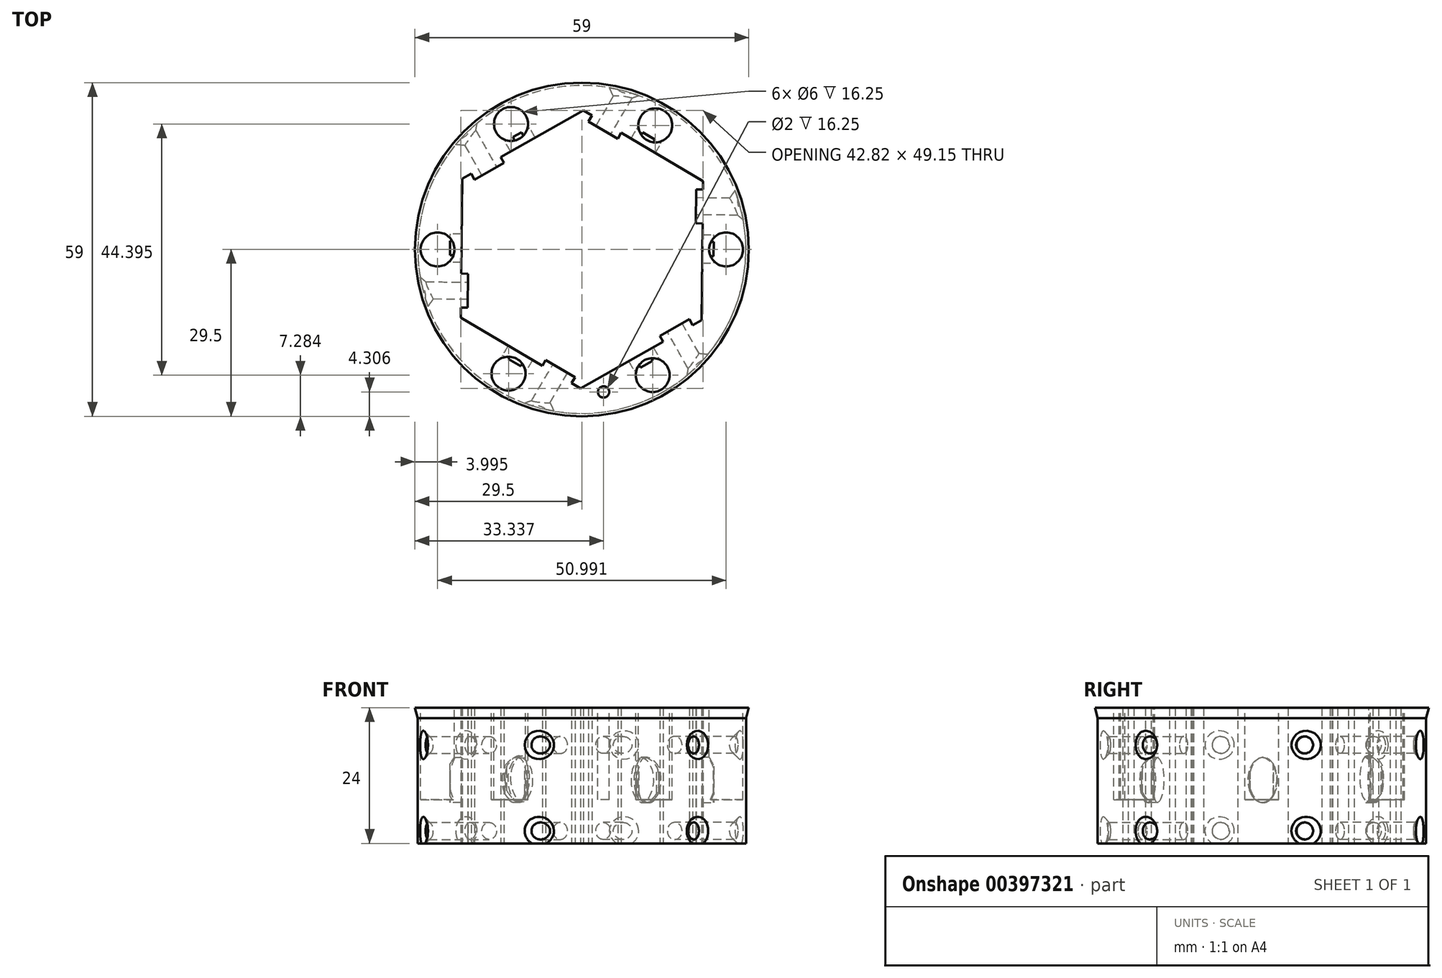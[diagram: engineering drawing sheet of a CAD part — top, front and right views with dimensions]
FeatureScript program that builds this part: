
annotation { "Feature Type Name" : "Feature", "Feature Type Description" : "" }
export const myFeature = defineFeature(function(context is Context, id is Id, definition is map)
    precondition{}
    {
        {
            var Q0;
            Q0=qCreatedBy(makeId("Top.planeOp"),FACE);
            var sketch = newSketch(context, id + "F0", { "sketchPlane" : qUnion([Q0])});
            skCircle(sketch, "E0", {"center": v(0, 0) * mm, "radius": 29 * mm});
            skCircle(sketch, "E1.cCircle", {"center": v(0, 0) * mm, "radius": 24.58 * mm, "construction": true});
            skLineSegment(sketch, "E1.0", {"start": v(-21.4, -12.07) * mm, "end": v(-21.16, 12.5) * mm});
            skLineSegment(sketch, "E1.1", {"start": v(-21.16, 12.5) * mm, "end": v(0.25, 24.58) * mm});
            skLineSegment(sketch, "E1.2", {"start": v(0.25, 24.58) * mm, "end": v(21.4, 12.07) * mm});
            skLineSegment(sketch, "E1.3", {"start": v(21.4, 12.07) * mm, "end": v(21.16, -12.5) * mm});
            skLineSegment(sketch, "E1.4", {"start": v(21.16, -12.5) * mm, "end": v(-0.25, -24.58) * mm});
            skLineSegment(sketch, "E1.5", {"start": v(-0.25, -24.58) * mm, "end": v(-21.4, -12.07) * mm});
            skSolve(sketch);
        }
        {
            var Q0;
            Q0=makeQuery(id+"F0.imprint","IMPRINT",FACE,{"disambiguationData":[TD([[makeQuery(id+"F0.imprint","IMPRINT",EDGE,{"derivedFrom":sQuery(id+"F0.wireOp",EDGE,"E0")}),1.0]])]});
            extrude(context, id + "F1", {"entities" : qUnion([Q0]), "depth" : 22 * mm});
        }
        {
            var Q0;
            Q0=makeQuery(id+"F1.opExtrude","CAP_FACE",FACE,{"disambiguationData":[OSD([sQuery(id+"F0.wireOp",EDGE,"E0"),sQuery(id+"F0.wireOp",EDGE,"E1.0"),sQuery(id+"F0.wireOp",EDGE,"E1.1"),sQuery(id+"F0.wireOp",EDGE,"E1.2"),sQuery(id+"F0.wireOp",EDGE,"E1.3"),sQuery(id+"F0.wireOp",EDGE,"E1.4"),sQuery(id+"F0.wireOp",EDGE,"E1.5")])],"isStart":false});
            var sketch = newSketch(context, id + "F2", { "sketchPlane" : qUnion([Q0])});
            skCircle(sketch, "E2.0", {"center": v(0, 0) * mm, "radius": 29.5 * mm});
            skSolve(sketch);
        }
        {
            var Q0;
            Q0=makeQuery(id+"F2.imprint","IMPRINT",FACE,{"disambiguationData":[TD([[makeQuery(id+"F2.imprint","IMPRINT",EDGE,{"derivedFrom":makeQuery(id+"F1.opExtrude","CAP_EDGE",EDGE,{"disambiguationData":[OSD([sQuery(id+"F0.wireOp",EDGE,"E0")])],"isStart":false})}),1.0]])]});
            var Q1;
            Q1=makeQuery(id+"F2.imprint","IMPRINT",FACE,{"disambiguationData":[TD([[makeQuery(id+"F2.imprint","IMPRINT",EDGE,{"derivedFrom":sQuery(id+"F2.wireOp",EDGE,"E2.0")}),1.0]])]});
            extrude(context, id + "F3", {"entities" : qUnion([Q0, Q1]), "operationType" : NewBodyOperationType.ADD, "depth" : 2 * mm});
        }
        {
            var Q0;
            Q0=makeQuery(id+"F3.opExtrude","CAP_FACE",FACE,{"disambiguationData":[OSD([sQuery(id+"F0.wireOp",EDGE,"E1.0"),sQuery(id+"F0.wireOp",EDGE,"E1.1"),sQuery(id+"F0.wireOp",EDGE,"E1.2"),sQuery(id+"F0.wireOp",EDGE,"E1.3"),sQuery(id+"F0.wireOp",EDGE,"E1.4"),sQuery(id+"F0.wireOp",EDGE,"E1.5"),sQuery(id+"F2.wireOp",EDGE,"E2.0")])],"isStart":false});
            var sketch = newSketch(context, id + "F4", { "sketchPlane" : qUnion([Q0])});
            skCircle(sketch, "E3", {"center": v(-12.53, 22.18) * mm, "radius": 3 * mm});
            skCircle(sketch, "E4", {"center": v(-25.5, 0) * mm, "radius": 3 * mm});
            skCircle(sketch, "E5", {"center": v(-12.97, -21.96) * mm, "radius": 3 * mm});
            skCircle(sketch, "E6", {"center": v(12.52, -22.22) * mm, "radius": 3 * mm});
            skCircle(sketch, "E7", {"center": v(25.49, 0) * mm, "radius": 3 * mm});
            skCircle(sketch, "E8", {"center": v(12.97, 21.94) * mm, "radius": 3 * mm});
            skCircle(sketch, "E9", {"center": v(3.84, -25.2) * mm, "radius": 1 * mm});
            skSolve(sketch);
        }
        {
            var Q0;
            Q0=makeQuery(id+"F4.imprint","IMPRINT",FACE,{"disambiguationData":[TD([[makeQuery(id+"F4.imprint","IMPRINT",EDGE,{"derivedFrom":sQuery(id+"F4.wireOp",EDGE,"E6")}),1.0]])]});
            var Q1;
            Q1=makeQuery(id+"F4.imprint","IMPRINT",FACE,{"disambiguationData":[TD([[makeQuery(id+"F4.imprint","IMPRINT",EDGE,{"derivedFrom":sQuery(id+"F4.wireOp",EDGE,"E5")}),1.0]])]});
            var Q2;
            Q2=makeQuery(id+"F4.imprint","IMPRINT",FACE,{"disambiguationData":[TD([[makeQuery(id+"F4.imprint","IMPRINT",EDGE,{"derivedFrom":sQuery(id+"F4.wireOp",EDGE,"E4")}),1.0]])]});
            var Q3;
            Q3=makeQuery(id+"F4.imprint","IMPRINT",FACE,{"disambiguationData":[TD([[makeQuery(id+"F4.imprint","IMPRINT",EDGE,{"derivedFrom":sQuery(id+"F4.wireOp",EDGE,"E3")}),1.0]])]});
            var Q4;
            Q4=makeQuery(id+"F4.imprint","IMPRINT",FACE,{"disambiguationData":[TD([[makeQuery(id+"F4.imprint","IMPRINT",EDGE,{"derivedFrom":sQuery(id+"F4.wireOp",EDGE,"E8")}),1.0]])]});
            var Q5;
            Q5=makeQuery(id+"F4.imprint","IMPRINT",FACE,{"disambiguationData":[TD([[makeQuery(id+"F4.imprint","IMPRINT",EDGE,{"derivedFrom":sQuery(id+"F4.wireOp",EDGE,"E7")}),1.0]])]});
            var Q6;
            Q6=makeQuery(id+"F4.imprint","IMPRINT",FACE,{"disambiguationData":[TD([[makeQuery(id+"F4.imprint","IMPRINT",EDGE,{"derivedFrom":sQuery(id+"F4.wireOp",EDGE,"E9")}),1.0]])]});
            var Q7;
            Q7=sQuery(id+"F4.wireOp",EDGE,"E3");
            var Q8;
            Q8=sQuery(id+"F4.wireOp",EDGE,"E5");
            var Q9;
            Q9=sQuery(id+"F4.wireOp",EDGE,"E9");
            var Q10;
            Q10=sQuery(id+"F4.wireOp",EDGE,"E6");
            var Q11;
            Q11=sQuery(id+"F4.wireOp",EDGE,"E7");
            var Q12;
            Q12=sQuery(id+"F4.wireOp",EDGE,"E8");
            var Q13;
            Q13=sQuery(id+"F4.wireOp",EDGE,"E4");
            extrude(context, id + "F5", {"entities" : qUnion([Q0, Q1, Q2, Q3, Q4, Q5, Q6]), "operationType" : NewBodyOperationType.REMOVE, "surfaceEntities" : qUnion([Q7, Q8, Q9, Q10, Q11, Q12, Q13]), "oppositeDirection" : true, "depth" : 16.25 * mm});
        }
        {
            var Q0;
            {var subQ0=sQuery(id+"F0.wireOp",EDGE,"E1.4");Q0=makeQuery(id+"F3.boolean.opBoolean","MERGE",FACE,{"derivedFrom":[makeQuery(id+"F1.opExtrude","SWEPT_FACE",FACE,{"disambiguationData":[OSD([subQ0])]}),makeQuery(id+"F3.opExtrude","SWEPT_FACE",FACE,{"disambiguationData":[OSD([subQ0])]})]});}
            var sketch = newSketch(context, id + "F6", { "sketchPlane" : qUnion([Q0])});
            skLineSegment(sketch, "E10", {"start": v(0, 24) * mm, "end": v(0, -1.6) * mm, "construction": true});
            skPoint(sketch, "E10.endSnap0", {"position": v(0, 24) * mm});
            skEllipse(sketch, "E11", {"center": v(0, 11.2) * mm, "majorRadius": 4 * mm, "minorRadius": 2.5 * mm, "majorAxis": v(0, 1)});
            skLineSegment(sketch, "E12", {"start": v(-7.5, 24) * mm, "end": v(-7.5, 0) * mm, "construction": true});
            skCircle(sketch, "E13", {"center": v(-7.5, 17.4) * mm, "radius": 1.5 * mm});
            skCircle(sketch, "E14", {"center": v(-7.5, 2.2) * mm, "radius": 1.5 * mm});
            skSolve(sketch);
        }
        {
            var Q0;
            Q0=makeQuery(id+"F6.imprint","IMPRINT",FACE,{"disambiguationData":[TD([[makeQuery(id+"F6.imprint","IMPRINT",EDGE,{"derivedFrom":sQuery(id+"F6.wireOp",EDGE,"E11")}),1.0]])]});
            var Q1;
            Q1=sQuery(id+"F6.wireOp",EDGE,"E13");
            extrude(context, id + "F7", {"entities" : qUnion([Q0]), "operationType" : NewBodyOperationType.REMOVE, "surfaceEntities" : qUnion([Q1]), "oppositeDirection" : true, "depth" : 2 * mm});
        }
        {
            var Q0;
            {var subQ0=sQuery(id+"F0.wireOp",EDGE,"E1.4");Q0=makeQuery(id+"F3.boolean.opBoolean","MERGE",FACE,{"derivedFrom":[makeQuery(id+"F1.opExtrude","SWEPT_FACE",FACE,{"disambiguationData":[OSD([subQ0])]}),makeQuery(id+"F3.opExtrude","SWEPT_FACE",FACE,{"disambiguationData":[OSD([subQ0])]})]});}
            var sketch = newSketch(context, id + "F8", { "sketchPlane" : qUnion([Q0])});
            skPoint(sketch, "E15.1", {"position": v(0, 24) * mm});
            skCircle(sketch, "E15.4", {"center": v(-7.5, 17.4) * mm, "radius": 1.5 * mm});
            skCircle(sketch, "E15.5", {"center": v(-7.5, 2.2) * mm, "radius": 1.5 * mm});
            skSolve(sketch);
        }
        {
            var Q0;
            Q0=makeQuery(id+"F8.imprint","IMPRINT",FACE,{"disambiguationData":[TD([[makeQuery(id+"F8.imprint","IMPRINT",EDGE,{"derivedFrom":sQuery(id+"F8.wireOp",EDGE,"E15.5")}),1.0]])]});
            var Q1;
            Q1=makeQuery(id+"F8.imprint","IMPRINT",FACE,{"disambiguationData":[TD([[makeQuery(id+"F8.imprint","IMPRINT",EDGE,{"derivedFrom":sQuery(id+"F8.wireOp",EDGE,"E15.4")}),1.0]])]});
            extrude(context, id + "F9", {"entities" : qUnion([Q0, Q1]), "operationType" : NewBodyOperationType.REMOVE, "oppositeDirection" : true, "depth" : 10 * mm, "hasSecondDirection" : true, "secondDirectionOppositeDirection" : false, "secondDirectionDepth" : 5 * mm});
        }
        {
            var Q0;
            {var subQ0=sQuery(id+"F0.wireOp",EDGE,"E1.4");Q0=makeQuery(id+"F3.boolean.opBoolean","MERGE",FACE,{"derivedFrom":[makeQuery(id+"F1.opExtrude","SWEPT_FACE",FACE,{"disambiguationData":[OSD([subQ0])]}),makeQuery(id+"F3.opExtrude","SWEPT_FACE",FACE,{"disambiguationData":[OSD([subQ0])]})]});}
            var sketch = newSketch(context, id + "F10", { "sketchPlane" : qUnion([Q0])});
            skLineSegment(sketch, "E16.bottom", {"start": v(-4.5, 24) * mm, "end": v(-10.5, 24) * mm});
            skLineSegment(sketch, "E16.top", {"start": v(-4.5, 0) * mm, "end": v(-10.5, 0) * mm});
            skLineSegment(sketch, "E16.left", {"start": v(-4.5, 24) * mm, "end": v(-4.5, 0) * mm});
            skLineSegment(sketch, "E16.right", {"start": v(-10.5, 24) * mm, "end": v(-10.5, 0) * mm});
            skSolve(sketch);
        }
        {
            var Q0;
            Q0=makeQuery(id+"F10.imprint","IMPRINT",FACE,{"disambiguationData":[TD([[makeQuery(id+"F10.imprint","IMPRINT",EDGE,{"derivedFrom":sQuery(id+"F10.wireOp",EDGE,"E16.bottom")}),-1.0]])]});
            extrude(context, id + "F11", {"entities" : qUnion([Q0]), "operationType" : NewBodyOperationType.ADD, "depth" : 1.2 * mm});
        }
        {
            var Q0;
            {var subQ0=sQuery(id+"F0.wireOp",EDGE,"E1.5");Q0=makeQuery(id+"F3.boolean.opBoolean","MERGE",FACE,{"derivedFrom":[makeQuery(id+"F1.opExtrude","SWEPT_FACE",FACE,{"disambiguationData":[OSD([subQ0])]}),makeQuery(id+"F3.opExtrude","SWEPT_FACE",FACE,{"disambiguationData":[OSD([subQ0])]})]});}
            var sketch = newSketch(context, id + "F12", { "sketchPlane" : qUnion([Q0])});
            skLineSegment(sketch, "E17", {"start": v(0, 24) * mm, "end": v(0, 0) * mm, "construction": true});
            skLineSegment(sketch, "E18", {"start": v(0.05, 24) * mm, "end": v(0.05, -1.6) * mm, "construction": true});
            skPoint(sketch, "E18.endSnap0", {"position": v(0.05, 24) * mm});
            skEllipse(sketch, "E19", {"center": v(0.05, 11.2) * mm, "majorRadius": 4 * mm, "minorRadius": 2.5 * mm, "majorAxis": v(0, 1)});
            skLineSegment(sketch, "E20", {"start": v(-7.45, 24) * mm, "end": v(-7.45, 0) * mm, "construction": true});
            skCircle(sketch, "E21", {"center": v(-7.45, 17.4) * mm, "radius": 1.5 * mm});
            skCircle(sketch, "E22", {"center": v(-7.45, 2.2) * mm, "radius": 1.5 * mm});
            skSolve(sketch);
        }
        {
            var Q0;
            {var subQ0=sQuery(id+"F0.wireOp",EDGE,"E1.3");Q0=makeQuery(id+"F3.boolean.opBoolean","MERGE",FACE,{"derivedFrom":[makeQuery(id+"F1.opExtrude","SWEPT_FACE",FACE,{"disambiguationData":[OSD([subQ0])]}),makeQuery(id+"F3.opExtrude","SWEPT_FACE",FACE,{"disambiguationData":[OSD([subQ0])]})]});}
            var sketch = newSketch(context, id + "F13", { "sketchPlane" : qUnion([Q0])});
            skLineSegment(sketch, "E23", {"start": v(-0.37, 24) * mm, "end": v(-0.37, 0) * mm, "construction": true});
            skLineSegment(sketch, "E24", {"start": v(-0.32, 24) * mm, "end": v(-0.32, -1.6) * mm, "construction": true});
            skPoint(sketch, "E24.endSnap0", {"position": v(-0.32, 24) * mm});
            skEllipse(sketch, "E25", {"center": v(-0.32, 11.2) * mm, "majorRadius": 4 * mm, "minorRadius": 2.5 * mm, "majorAxis": v(0, 1)});
            skLineSegment(sketch, "E26", {"start": v(-7.82, 24) * mm, "end": v(-7.82, 0) * mm, "construction": true});
            skCircle(sketch, "E27", {"center": v(-7.82, 17.4) * mm, "radius": 1.5 * mm});
            skCircle(sketch, "E28", {"center": v(-7.82, 2.2) * mm, "radius": 1.5 * mm});
            skSolve(sketch);
        }
        {
            var Q0;
            {var subQ0=sQuery(id+"F0.wireOp",EDGE,"E1.0");Q0=makeQuery(id+"F3.boolean.opBoolean","MERGE",FACE,{"derivedFrom":[makeQuery(id+"F1.opExtrude","SWEPT_FACE",FACE,{"disambiguationData":[OSD([subQ0])]}),makeQuery(id+"F3.opExtrude","SWEPT_FACE",FACE,{"disambiguationData":[OSD([subQ0])]})]});}
            var sketch = newSketch(context, id + "F14", { "sketchPlane" : qUnion([Q0])});
            skLineSegment(sketch, "E29", {"start": v(0, 24) * mm, "end": v(0, 0) * mm, "construction": true});
            skLineSegment(sketch, "E30", {"start": v(0, 24) * mm, "end": v(0, -1.6) * mm, "construction": true});
            skPoint(sketch, "E30.endSnap0", {"position": v(0, 24) * mm});
            skEllipse(sketch, "E31", {"center": v(0, 11.2) * mm, "majorRadius": 4 * mm, "minorRadius": 2.5 * mm, "majorAxis": v(0, 1)});
            skLineSegment(sketch, "E32", {"start": v(-7.5, 24) * mm, "end": v(-7.5, 0) * mm, "construction": true});
            skCircle(sketch, "E33", {"center": v(-7.5, 17.4) * mm, "radius": 1.5 * mm});
            skCircle(sketch, "E34", {"center": v(-7.5, 2.2) * mm, "radius": 1.5 * mm});
            skSolve(sketch);
        }
        {
            var Q0;
            {var subQ0=sQuery(id+"F0.wireOp",EDGE,"E1.1");Q0=makeQuery(id+"F3.boolean.opBoolean","MERGE",FACE,{"derivedFrom":[makeQuery(id+"F1.opExtrude","SWEPT_FACE",FACE,{"disambiguationData":[OSD([subQ0])]}),makeQuery(id+"F3.opExtrude","SWEPT_FACE",FACE,{"disambiguationData":[OSD([subQ0])]})]});}
            var sketch = newSketch(context, id + "F15", { "sketchPlane" : qUnion([Q0])});
            skLineSegment(sketch, "E35", {"start": v(0, 24) * mm, "end": v(0, 0) * mm, "construction": true});
            skLineSegment(sketch, "E36", {"start": v(0.02, 24.28) * mm, "end": v(0.02, -1.32) * mm, "construction": true});
            skPoint(sketch, "E36.endSnap0", {"position": v(0.02, 24.28) * mm});
            skEllipse(sketch, "E37", {"center": v(0.02, 11.48) * mm, "majorRadius": 4 * mm, "minorRadius": 2.5 * mm, "majorAxis": v(0, 1)});
            skLineSegment(sketch, "E38", {"start": v(-7.48, 24) * mm, "end": v(-7.48, 0) * mm, "construction": true});
            skCircle(sketch, "E39", {"center": v(-7.48, 17.4) * mm, "radius": 1.5 * mm});
            skCircle(sketch, "E40", {"center": v(-7.48, 2.2) * mm, "radius": 1.5 * mm});
            skSolve(sketch);
        }
        {
            var Q0;
            {var subQ0=sQuery(id+"F0.wireOp",EDGE,"E1.2");Q0=makeQuery(id+"F3.boolean.opBoolean","MERGE",FACE,{"derivedFrom":[makeQuery(id+"F1.opExtrude","SWEPT_FACE",FACE,{"disambiguationData":[OSD([subQ0])]}),makeQuery(id+"F3.opExtrude","SWEPT_FACE",FACE,{"disambiguationData":[OSD([subQ0])]})]});}
            var sketch = newSketch(context, id + "F16", { "sketchPlane" : qUnion([Q0])});
            skLineSegment(sketch, "E41", {"start": v(0, 24) * mm, "end": v(0, 0) * mm, "construction": true});
            skLineSegment(sketch, "E42", {"start": v(-0.06, 24) * mm, "end": v(-0.06, 0) * mm, "construction": true});
            skLineSegment(sketch, "E43", {"start": v(0, 24) * mm, "end": v(0, -1.6) * mm, "construction": true});
            skPoint(sketch, "E43.endSnap0", {"position": v(0, 24) * mm});
            skEllipse(sketch, "E44", {"center": v(0, 11.2) * mm, "majorRadius": 4 * mm, "minorRadius": 2.5 * mm, "majorAxis": v(0, 1)});
            skLineSegment(sketch, "E45", {"start": v(-7.5, 24) * mm, "end": v(-7.5, 0) * mm, "construction": true});
            skCircle(sketch, "E46", {"center": v(-7.5, 17.4) * mm, "radius": 1.5 * mm});
            skCircle(sketch, "E47", {"center": v(-7.5, 2.2) * mm, "radius": 1.5 * mm});
            skSolve(sketch);
        }
        {
            var Q0;
            Q0=makeQuery(id+"F16.imprint","IMPRINT",FACE,{"disambiguationData":[TD([[makeQuery(id+"F16.imprint","IMPRINT",EDGE,{"derivedFrom":sQuery(id+"F16.wireOp",EDGE,"E47")}),1.0]])]});
            var Q1;
            Q1=makeQuery(id+"F16.imprint","IMPRINT",FACE,{"disambiguationData":[TD([[makeQuery(id+"F16.imprint","IMPRINT",EDGE,{"derivedFrom":sQuery(id+"F16.wireOp",EDGE,"E46")}),1.0]])]});
            var Q2;
            Q2=sQuery(id+"F16.wireOp",EDGE,"E46");
            var Q3;
            Q3=sQuery(id+"F16.wireOp",EDGE,"E47");
            extrude(context, id + "F17", {"entities" : qUnion([Q0, Q1]), "operationType" : NewBodyOperationType.REMOVE, "surfaceEntities" : qUnion([Q2, Q3]), "oppositeDirection" : true, "depth" : 10 * mm, "hasSecondDirection" : true, "secondDirectionOppositeDirection" : false, "secondDirectionDepth" : 10 * mm});
        }
        {
            var Q0;
            Q0 = qSketchRegion(id + "F16", true);
            extrude(context, id + "F18", {"entities" : qUnion([Q0]), "operationType" : NewBodyOperationType.REMOVE, "oppositeDirection" : true, "depth" : 2 * mm});
        }
        {
            var Q0;
            Q0=makeQuery(id+"F15.imprint","IMPRINT",FACE,{"disambiguationData":[TD([[makeQuery(id+"F15.imprint","IMPRINT",EDGE,{"derivedFrom":sQuery(id+"F15.wireOp",EDGE,"E40")}),1.0]])]});
            var Q1;
            Q1=makeQuery(id+"F15.imprint","IMPRINT",FACE,{"disambiguationData":[TD([[makeQuery(id+"F15.imprint","IMPRINT",EDGE,{"derivedFrom":sQuery(id+"F15.wireOp",EDGE,"E39")}),1.0]])]});
            extrude(context, id + "F19", {"entities" : qUnion([Q0, Q1]), "operationType" : NewBodyOperationType.REMOVE, "oppositeDirection" : true, "depth" : 10 * mm, "hasSecondDirection" : true, "secondDirectionOppositeDirection" : false, "secondDirectionDepth" : 10 * mm});
        }
        {
            var Q0;
            Q0=makeQuery(id+"F13.imprint","IMPRINT",FACE,{"disambiguationData":[TD([[makeQuery(id+"F13.imprint","IMPRINT",EDGE,{"derivedFrom":sQuery(id+"F13.wireOp",EDGE,"E27")}),1.0]])]});
            var Q1;
            Q1=makeQuery(id+"F13.imprint","IMPRINT",FACE,{"disambiguationData":[TD([[makeQuery(id+"F13.imprint","IMPRINT",EDGE,{"derivedFrom":sQuery(id+"F13.wireOp",EDGE,"E28")}),1.0]])]});
            var Q2;
            Q2=sQuery(id+"F13.wireOp",EDGE,"E27");
            var Q3;
            Q3=sQuery(id+"F13.wireOp",EDGE,"E28");
            extrude(context, id + "F20", {"entities" : qUnion([Q0, Q1]), "operationType" : NewBodyOperationType.REMOVE, "surfaceEntities" : qUnion([Q2, Q3]), "oppositeDirection" : true, "depth" : 10 * mm, "hasSecondDirection" : true, "secondDirectionOppositeDirection" : false, "secondDirectionDepth" : 10 * mm});
        }
        {
            var Q0;
            Q0=makeQuery(id+"F12.imprint","IMPRINT",FACE,{"disambiguationData":[TD([[makeQuery(id+"F12.imprint","IMPRINT",EDGE,{"derivedFrom":sQuery(id+"F12.wireOp",EDGE,"E21")}),1.0]])]});
            var Q1;
            Q1=makeQuery(id+"F12.imprint","IMPRINT",FACE,{"disambiguationData":[TD([[makeQuery(id+"F12.imprint","IMPRINT",EDGE,{"derivedFrom":sQuery(id+"F12.wireOp",EDGE,"E22")}),1.0]])]});
            var Q2;
            Q2=sQuery(id+"F12.wireOp",EDGE,"E21");
            extrude(context, id + "F21", {"entities" : qUnion([Q0, Q1]), "operationType" : NewBodyOperationType.REMOVE, "surfaceEntities" : qUnion([Q2]), "oppositeDirection" : true, "depth" : 10 * mm, "hasSecondDirection" : true, "secondDirectionOppositeDirection" : false, "secondDirectionDepth" : 10 * mm});
        }
        {
            var Q0;
            Q0 = qSketchRegion(id + "F12", true);
            extrude(context, id + "F22", {"entities" : qUnion([Q0]), "operationType" : NewBodyOperationType.REMOVE, "oppositeDirection" : true, "depth" : 2 * mm});
        }
        {
            var Q0;
            Q0 = qSketchRegion(id + "F14", true);
            extrude(context, id + "F23", {"entities" : qUnion([Q0]), "operationType" : NewBodyOperationType.REMOVE, "oppositeDirection" : true, "depth" : 2 * mm});
        }
        {
            var Q0;
            Q0 = qSketchRegion(id + "F15", true);
            extrude(context, id + "F24", {"entities" : qUnion([Q0]), "operationType" : NewBodyOperationType.REMOVE, "oppositeDirection" : true, "depth" : 2 * mm});
        }
        {
            var Q0;
            Q0 = qSketchRegion(id + "F13", true);
            extrude(context, id + "F25", {"entities" : qUnion([Q0]), "operationType" : NewBodyOperationType.REMOVE, "oppositeDirection" : true, "depth" : 2 * mm});
        }
        {
            var Q0;
            {var subQ0=sQuery(id+"F0.wireOp",EDGE,"E1.0");Q0=makeQuery(id+"F3.boolean.opBoolean","MERGE",FACE,{"derivedFrom":[makeQuery(id+"F1.opExtrude","SWEPT_FACE",FACE,{"disambiguationData":[OSD([subQ0])]}),makeQuery(id+"F3.opExtrude","SWEPT_FACE",FACE,{"disambiguationData":[OSD([subQ0])]})]});}
            var sketch = newSketch(context, id + "F26", { "sketchPlane" : qUnion([Q0])});
            skLineSegment(sketch, "E48.bottom", {"start": v(-10.5, 24) * mm, "end": v(-4.5, 24) * mm});
            skLineSegment(sketch, "E48.top", {"start": v(-10.5, 0) * mm, "end": v(-4.5, 0) * mm});
            skLineSegment(sketch, "E48.left", {"start": v(-10.5, 24) * mm, "end": v(-10.5, 0) * mm});
            skLineSegment(sketch, "E48.right", {"start": v(-4.5, 24) * mm, "end": v(-4.5, 0) * mm});
            skSolve(sketch);
        }
        {
            var Q0;
            Q0=makeQuery(id+"F26.imprint","IMPRINT",FACE,{"disambiguationData":[TD([[makeQuery(id+"F26.imprint","IMPRINT",EDGE,{"derivedFrom":sQuery(id+"F26.wireOp",EDGE,"E48.bottom")}),-1.0]])]});
            extrude(context, id + "F27", {"entities" : qUnion([Q0]), "operationType" : NewBodyOperationType.ADD, "depth" : 1.2 * mm});
        }
        {
            var Q0;
            {var subQ0=sQuery(id+"F0.wireOp",EDGE,"E1.1");Q0=makeQuery(id+"F3.boolean.opBoolean","MERGE",FACE,{"derivedFrom":[makeQuery(id+"F1.opExtrude","SWEPT_FACE",FACE,{"disambiguationData":[OSD([subQ0])]}),makeQuery(id+"F3.opExtrude","SWEPT_FACE",FACE,{"disambiguationData":[OSD([subQ0])]})]});}
            var sketch = newSketch(context, id + "F28", { "sketchPlane" : qUnion([Q0])});
            skLineSegment(sketch, "E49.bottom", {"start": v(-10.48, 24) * mm, "end": v(-4.48, 24) * mm});
            skLineSegment(sketch, "E49.top", {"start": v(-10.48, 0) * mm, "end": v(-4.48, 0) * mm});
            skLineSegment(sketch, "E49.left", {"start": v(-10.48, 24) * mm, "end": v(-10.48, 0) * mm});
            skLineSegment(sketch, "E49.right", {"start": v(-4.48, 24) * mm, "end": v(-4.48, 0) * mm});
            skSolve(sketch);
        }
        {
            var Q0;
            Q0=makeQuery(id+"F28.imprint","IMPRINT",FACE,{"disambiguationData":[TD([[makeQuery(id+"F28.imprint","IMPRINT",EDGE,{"derivedFrom":sQuery(id+"F28.wireOp",EDGE,"E49.bottom")}),-1.0]])]});
            extrude(context, id + "F29", {"entities" : qUnion([Q0]), "operationType" : NewBodyOperationType.ADD, "depth" : 1.2 * mm});
        }
        {
            var Q0;
            {var subQ0=sQuery(id+"F0.wireOp",EDGE,"E1.5");Q0=makeQuery(id+"F3.boolean.opBoolean","MERGE",FACE,{"derivedFrom":[makeQuery(id+"F1.opExtrude","SWEPT_FACE",FACE,{"disambiguationData":[OSD([subQ0])]}),makeQuery(id+"F3.opExtrude","SWEPT_FACE",FACE,{"disambiguationData":[OSD([subQ0])]})]});}
            var sketch = newSketch(context, id + "F30", { "sketchPlane" : qUnion([Q0])});
            skLineSegment(sketch, "E50.bottom", {"start": v(-4.45, 24) * mm, "end": v(-10.45, 24) * mm});
            skLineSegment(sketch, "E50.top", {"start": v(-4.45, 0) * mm, "end": v(-10.45, 0) * mm});
            skLineSegment(sketch, "E50.left", {"start": v(-4.45, 24) * mm, "end": v(-4.45, 0) * mm});
            skLineSegment(sketch, "E50.right", {"start": v(-10.45, 24) * mm, "end": v(-10.45, 0) * mm});
            skSolve(sketch);
        }
        {
            var Q0;
            Q0=makeQuery(id+"F30.imprint","IMPRINT",FACE,{"disambiguationData":[TD([[makeQuery(id+"F30.imprint","IMPRINT",EDGE,{"derivedFrom":sQuery(id+"F30.wireOp",EDGE,"E50.bottom")}),-1.0]])]});
            extrude(context, id + "F31", {"entities" : qUnion([Q0]), "operationType" : NewBodyOperationType.ADD, "depth" : 1.2 * mm});
        }
        {
            var Q0;
            {var subQ0=sQuery(id+"F0.wireOp",EDGE,"E1.3");Q0=makeQuery(id+"F3.boolean.opBoolean","MERGE",FACE,{"derivedFrom":[makeQuery(id+"F1.opExtrude","SWEPT_FACE",FACE,{"disambiguationData":[OSD([subQ0])]}),makeQuery(id+"F3.opExtrude","SWEPT_FACE",FACE,{"disambiguationData":[OSD([subQ0])]})]});}
            var sketch = newSketch(context, id + "F32", { "sketchPlane" : qUnion([Q0])});
            skLineSegment(sketch, "E51.bottom", {"start": v(-4.82, 24) * mm, "end": v(-10.82, 24) * mm});
            skLineSegment(sketch, "E51.top", {"start": v(-4.82, 0) * mm, "end": v(-10.82, 0) * mm});
            skLineSegment(sketch, "E51.left", {"start": v(-4.82, 24) * mm, "end": v(-4.82, 0) * mm});
            skLineSegment(sketch, "E51.right", {"start": v(-10.82, 24) * mm, "end": v(-10.82, 0) * mm});
            skSolve(sketch);
        }
        {
            var Q0;
            Q0=makeQuery(id+"F32.imprint","IMPRINT",FACE,{"disambiguationData":[TD([[makeQuery(id+"F32.imprint","IMPRINT",EDGE,{"derivedFrom":sQuery(id+"F32.wireOp",EDGE,"E51.bottom")}),-1.0]])]});
            extrude(context, id + "F33", {"entities" : qUnion([Q0]), "operationType" : NewBodyOperationType.ADD, "depth" : 1.2 * mm});
        }
        {
            var Q0;
            {var subQ0=sQuery(id+"F0.wireOp",EDGE,"E1.2");Q0=makeQuery(id+"F3.boolean.opBoolean","MERGE",FACE,{"derivedFrom":[makeQuery(id+"F1.opExtrude","SWEPT_FACE",FACE,{"disambiguationData":[OSD([subQ0])]}),makeQuery(id+"F3.opExtrude","SWEPT_FACE",FACE,{"disambiguationData":[OSD([subQ0])]})]});}
            var sketch = newSketch(context, id + "F34", { "sketchPlane" : qUnion([Q0])});
            skLineSegment(sketch, "E52.bottom", {"start": v(-10.5, 24) * mm, "end": v(-4.5, 24) * mm});
            skLineSegment(sketch, "E52.top", {"start": v(-10.5, 0) * mm, "end": v(-4.5, 0) * mm});
            skLineSegment(sketch, "E52.left", {"start": v(-10.5, 24) * mm, "end": v(-10.5, 0) * mm});
            skLineSegment(sketch, "E52.right", {"start": v(-4.5, 24) * mm, "end": v(-4.5, 0) * mm});
            skSolve(sketch);
        }
        {
            var Q0;
            Q0=makeQuery(id+"F34.imprint","IMPRINT",FACE,{"disambiguationData":[TD([[makeQuery(id+"F34.imprint","IMPRINT",EDGE,{"derivedFrom":sQuery(id+"F34.wireOp",EDGE,"E52.bottom")}),-1.0]])]});
            extrude(context, id + "F35", {"entities" : qUnion([Q0]), "operationType" : NewBodyOperationType.ADD, "depth" : 1.2 * mm});
        }
        {
            var Q0;
            Q0=makeQuery(id+"F3.opExtrude","CAP_EDGE",EDGE,{"disambiguationData":[OSD([sQuery(id+"F2.wireOp",EDGE,"E2.0")])],"isStart":true});
            chamfer(context, id + "F36", {"entities" : qUnion([Q0]), "chamferType" : ChamferType.OFFSET_ANGLE, "width" : 2 * mm, "oppositeDirection" : false, "angle" : 15 * degree, "tangentPropagation" : true});
        }
        {
            var Q0;
            Q0=makeQuery(id+"F19.boolean.opBoolean","INTERSECT",EDGE,{"derivedFrom":[makeQuery(id+"F1.opExtrude","SWEPT_FACE",FACE,{"disambiguationData":[OSD([sQuery(id+"F0.wireOp",EDGE,"E0")])]}),makeQuery(id+"F19.opExtrude","SWEPT_FACE",FACE,{"disambiguationData":[OSD([sQuery(id+"F15.wireOp",EDGE,"E39")])]})]});
            var Q1;
            Q1=makeQuery(id+"F19.boolean.opBoolean","INTERSECT",EDGE,{"derivedFrom":[makeQuery(id+"F1.opExtrude","SWEPT_FACE",FACE,{"disambiguationData":[OSD([sQuery(id+"F0.wireOp",EDGE,"E0")])]}),makeQuery(id+"F19.opExtrude","SWEPT_FACE",FACE,{"disambiguationData":[OSD([sQuery(id+"F15.wireOp",EDGE,"E40")])]})]});
            chamfer(context, id + "F37", {"entities" : qUnion([Q0, Q1]), "width" : 1 * mm, "tangentPropagation" : true});
        }
        {
            var Q0;
            Q0=makeQuery(id+"F17.boolean.opBoolean","INTERSECT",EDGE,{"derivedFrom":[makeQuery(id+"F1.opExtrude","SWEPT_FACE",FACE,{"disambiguationData":[OSD([sQuery(id+"F0.wireOp",EDGE,"E0")])]}),makeQuery(id+"F17.opExtrude","SWEPT_FACE",FACE,{"disambiguationData":[OSD([sQuery(id+"F16.wireOp",EDGE,"E46")])]})]});
            var Q1;
            Q1=makeQuery(id+"F17.boolean.opBoolean","INTERSECT",EDGE,{"derivedFrom":[makeQuery(id+"F1.opExtrude","SWEPT_FACE",FACE,{"disambiguationData":[OSD([sQuery(id+"F0.wireOp",EDGE,"E0")])]}),makeQuery(id+"F17.opExtrude","SWEPT_FACE",FACE,{"disambiguationData":[OSD([sQuery(id+"F16.wireOp",EDGE,"E47")])]})]});
            chamfer(context, id + "F38", {"entities" : qUnion([Q0, Q1]), "width" : 1 * mm, "tangentPropagation" : true});
        }
        {
            var Q0;
            Q0=makeQuery(id+"F20.boolean.opBoolean","INTERSECT",EDGE,{"derivedFrom":[makeQuery(id+"F1.opExtrude","SWEPT_FACE",FACE,{"disambiguationData":[OSD([sQuery(id+"F0.wireOp",EDGE,"E0")])]}),makeQuery(id+"F20.opExtrude","SWEPT_FACE",FACE,{"disambiguationData":[OSD([sQuery(id+"F13.wireOp",EDGE,"E28")])]})]});
            var Q1;
            Q1=makeQuery(id+"F20.boolean.opBoolean","INTERSECT",EDGE,{"derivedFrom":[makeQuery(id+"F1.opExtrude","SWEPT_FACE",FACE,{"disambiguationData":[OSD([sQuery(id+"F0.wireOp",EDGE,"E0")])]}),makeQuery(id+"F20.opExtrude","SWEPT_FACE",FACE,{"disambiguationData":[OSD([sQuery(id+"F13.wireOp",EDGE,"E27")])]})]});
            chamfer(context, id + "F39", {"entities" : qUnion([Q0, Q1]), "width" : 1 * mm, "tangentPropagation" : true});
        }
        {
            var Q0;
            Q0=makeQuery(id+"F9.boolean.opBoolean","INTERSECT",EDGE,{"derivedFrom":[makeQuery(id+"F1.opExtrude","SWEPT_FACE",FACE,{"disambiguationData":[OSD([sQuery(id+"F0.wireOp",EDGE,"E0")])]}),makeQuery(id+"F9.opExtrude","SWEPT_FACE",FACE,{"disambiguationData":[OSD([sQuery(id+"F8.wireOp",EDGE,"E15.5")])]})]});
            var Q1;
            Q1=makeQuery(id+"F9.boolean.opBoolean","INTERSECT",EDGE,{"derivedFrom":[makeQuery(id+"F1.opExtrude","SWEPT_FACE",FACE,{"disambiguationData":[OSD([sQuery(id+"F0.wireOp",EDGE,"E0")])]}),makeQuery(id+"F9.opExtrude","SWEPT_FACE",FACE,{"disambiguationData":[OSD([sQuery(id+"F8.wireOp",EDGE,"E15.4")])]})]});
            chamfer(context, id + "F40", {"entities" : qUnion([Q0, Q1]), "width" : 1 * mm, "tangentPropagation" : true});
        }
        {
            var Q0;
            Q0=makeQuery(id+"F21.boolean.opBoolean","INTERSECT",EDGE,{"derivedFrom":[makeQuery(id+"F1.opExtrude","SWEPT_FACE",FACE,{"disambiguationData":[OSD([sQuery(id+"F0.wireOp",EDGE,"E0")])]}),makeQuery(id+"F21.opExtrude","SWEPT_FACE",FACE,{"disambiguationData":[OSD([sQuery(id+"F12.wireOp",EDGE,"E22")])]})]});
            var Q1;
            Q1=makeQuery(id+"F21.boolean.opBoolean","INTERSECT",EDGE,{"derivedFrom":[makeQuery(id+"F1.opExtrude","SWEPT_FACE",FACE,{"disambiguationData":[OSD([sQuery(id+"F0.wireOp",EDGE,"E0")])]}),makeQuery(id+"F21.opExtrude","SWEPT_FACE",FACE,{"disambiguationData":[OSD([sQuery(id+"F12.wireOp",EDGE,"E21")])]})]});
            chamfer(context, id + "F41", {"entities" : qUnion([Q0, Q1]), "width" : 1 * mm, "tangentPropagation" : true});
        }
        {
            var Q0;
            Q0=makeQuery(id+"F23.boolean.opBoolean","COPY",FACE,{"derivedFrom":makeQuery(id+"F23.opExtrude","CAP_FACE",FACE,{"disambiguationData":[OSD([sQuery(id+"F14.wireOp",EDGE,"E33")])],"isStart":false})});
            var Q1;
            Q1=makeQuery(id+"F23.boolean.opBoolean","COPY",FACE,{"derivedFrom":makeQuery(id+"F23.opExtrude","CAP_FACE",FACE,{"disambiguationData":[OSD([sQuery(id+"F14.wireOp",EDGE,"E34")])],"isStart":false})});
            extrude(context, id + "F42", {"entities" : qUnion([Q0, Q1]), "operationType" : NewBodyOperationType.REMOVE, "oppositeDirection" : true, "depth" : 10 * mm, "hasSecondDirection" : true, "secondDirectionOppositeDirection" : false, "secondDirectionDepth" : 10 * mm});
        }
        {
            var Q0;
            Q0=makeQuery(id+"F42.boolean.opBoolean","INTERSECT",EDGE,{"derivedFrom":[makeQuery(id+"F1.opExtrude","SWEPT_FACE",FACE,{"disambiguationData":[OSD([sQuery(id+"F0.wireOp",EDGE,"E0")])]}),makeQuery(id+"F42.opExtrude","SWEPT_FACE",FACE,{"disambiguationData":[OSD([sQuery(id+"F14.wireOp",EDGE,"E33")])]})]});
            var Q1;
            Q1=makeQuery(id+"F42.boolean.opBoolean","INTERSECT",EDGE,{"derivedFrom":[makeQuery(id+"F1.opExtrude","SWEPT_FACE",FACE,{"disambiguationData":[OSD([sQuery(id+"F0.wireOp",EDGE,"E0")])]}),makeQuery(id+"F42.opExtrude","SWEPT_FACE",FACE,{"disambiguationData":[OSD([sQuery(id+"F14.wireOp",EDGE,"E34")])]})]});
            chamfer(context, id + "F43", {"entities" : qUnion([Q0, Q1]), "width" : 1 * mm, "tangentPropagation" : true});
        }
    });
